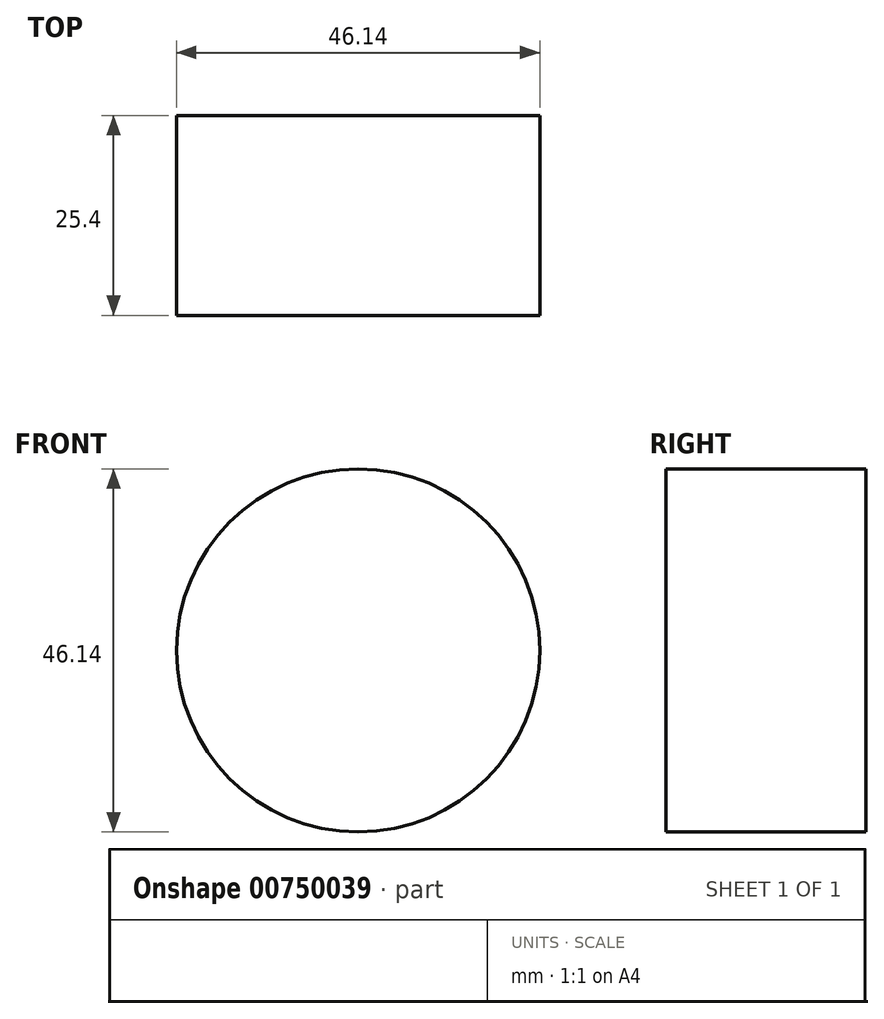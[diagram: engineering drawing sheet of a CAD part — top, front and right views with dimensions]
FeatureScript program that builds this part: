
annotation { "Feature Type Name" : "Feature", "Feature Type Description" : "" }
export const myFeature = defineFeature(function(context is Context, id is Id, definition is map)
    precondition{}
    {
        {
            var Q0;
            Q0=qCreatedBy(makeId("Front.planeOp"),FACE);
            var sketch = newSketch(context, id + "F0", { "sketchPlane" : qUnion([Q0])});
            skCircle(sketch, "E0", {"center": v(0, 0) * mm, "radius": 23.07 * mm});
            skSolve(sketch);
        }
        {
            var Q0;
            Q0 = qSketchRegion(id + "F0", true);
            extrude(context, id + "F1", {"entities" : qUnion([Q0]), "depth" : 25.4 * mm, "offsetDistance" : 25.4 * mm});
        }
    });
